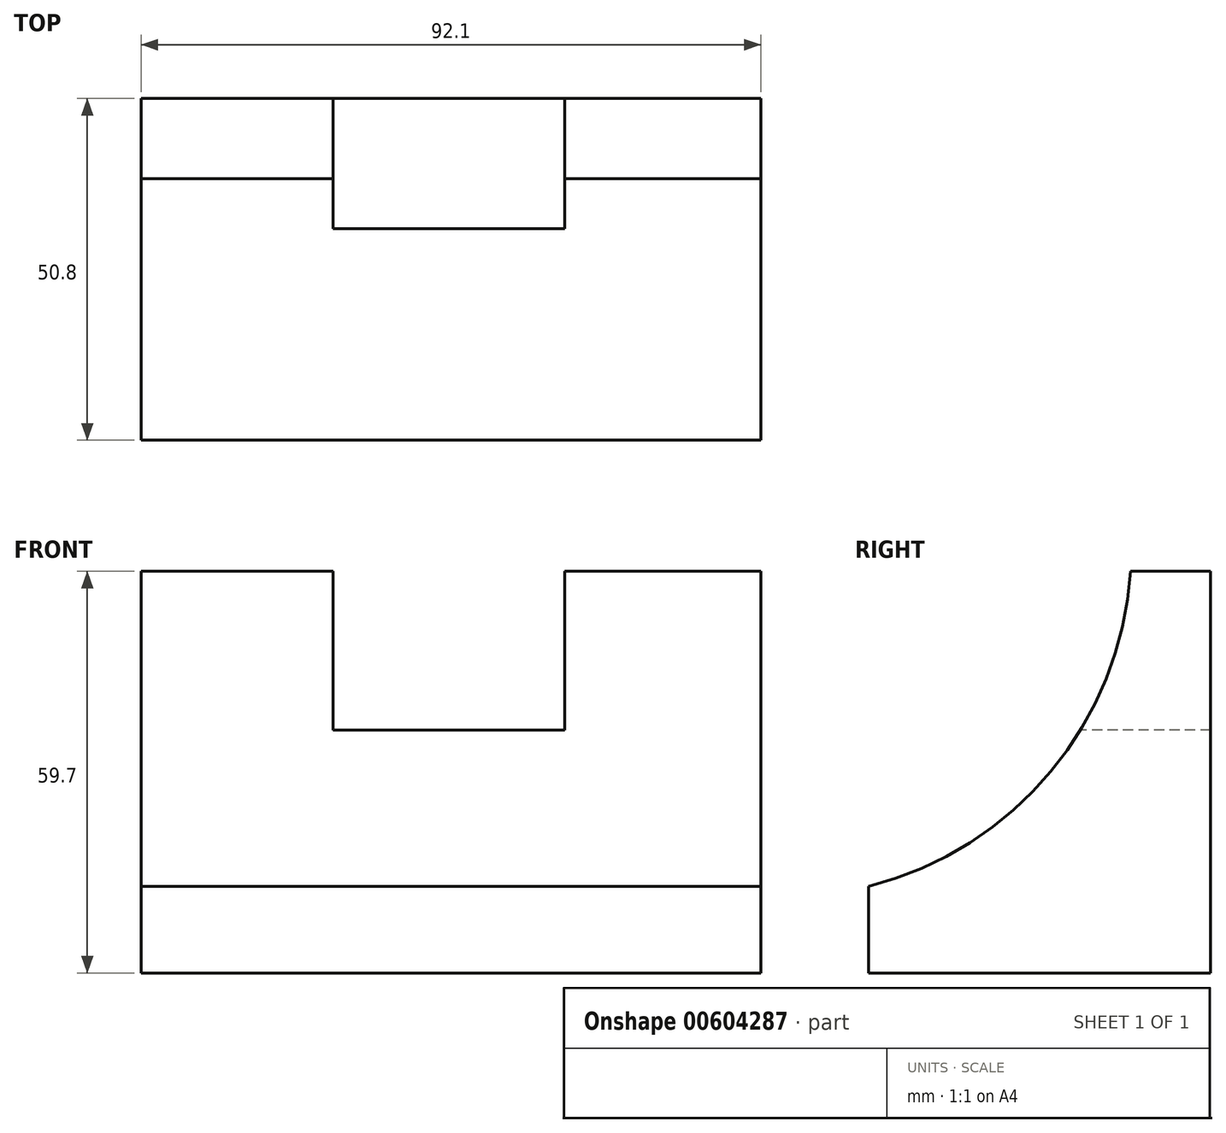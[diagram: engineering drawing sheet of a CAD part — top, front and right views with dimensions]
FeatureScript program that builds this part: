
annotation { "Feature Type Name" : "Feature", "Feature Type Description" : "" }
export const myFeature = defineFeature(function(context is Context, id is Id, definition is map)
    precondition{}
    {
        {
            var Q0;
            Q0=qCreatedBy(makeId("Front.planeOp"),FACE);
            var sketch = newSketch(context, id + "F0", { "sketchPlane" : qUnion([Q0])});
            skLineSegment(sketch, "E0.bottom", {"start": v(-72.72, 0) * mm, "end": v(19.38, 0) * mm});
            skLineSegment(sketch, "E0.top", {"start": v(-72.72, 59.7) * mm, "end": v(19.38, 59.7) * mm});
            skLineSegment(sketch, "E0.left", {"start": v(-72.72, 0) * mm, "end": v(-72.72, 59.7) * mm});
            skLineSegment(sketch, "E0.right", {"start": v(19.38, 0) * mm, "end": v(19.38, 59.7) * mm});
            skSolve(sketch);
        }
        {
            var Q0;
            Q0=makeQuery(id+"F0.imprint","IMPRINT",FACE,{"disambiguationData":[TD([[makeQuery(id+"F0.imprint","IMPRINT",EDGE,{"derivedFrom":sQuery(id+"F0.wireOp",EDGE,"E0.bottom")}),1.0]])]});
            extrude(context, id + "F1", {"entities" : qUnion([Q0]), "depth" : 25.4 * mm, "offsetDistance" : 25.4 * mm});
        }
        {
            var Q0;
            Q0=makeQuery(id+"F1.opExtrude","CAP_FACE",FACE,{"disambiguationData":[OSD([sQuery(id+"F0.wireOp",EDGE,"E0.bottom"),sQuery(id+"F0.wireOp",EDGE,"E0.top"),sQuery(id+"F0.wireOp",EDGE,"E0.left"),sQuery(id+"F0.wireOp",EDGE,"E0.right")])],"isStart":true});
            extrude(context, id + "F2", {"entities" : qUnion([Q0]), "operationType" : NewBodyOperationType.ADD, "depth" : 25.4 * mm, "offsetDistance" : 25.4 * mm});
        }
        {
            var Q0;
            {var subQ0=sQuery(id+"F0.wireOp",EDGE,"E0.right");Q0=makeQuery(id+"F2.boolean.opBoolean","MERGE",FACE,{"derivedFrom":[makeQuery(id+"F1.opExtrude","SWEPT_FACE",FACE,{"disambiguationData":[OSD([subQ0])]}),makeQuery(id+"F2.opExtrude","SWEPT_FACE",FACE,{"disambiguationData":[OSD([subQ0])]})]});}
            var sketch = newSketch(context, id + "F3", { "sketchPlane" : qUnion([Q0])});
            skArc(sketch, "E1", {"start": v(-25.4, 12.87) * mm, "mid": v(1.67, 29.95) * mm, "end": v(13.5, 59.7) * mm});
            skSolve(sketch);
        }
        {
            var Q0;
            Q0=makeQuery(id+"F1.opExtrude","CAP_FACE",FACE,{"disambiguationData":[OSD([sQuery(id+"F0.wireOp",EDGE,"E0.bottom"),sQuery(id+"F0.wireOp",EDGE,"E0.top"),sQuery(id+"F0.wireOp",EDGE,"E0.left"),sQuery(id+"F0.wireOp",EDGE,"E0.right")])],"isStart":false});
            var sketch = newSketch(context, id + "F4", { "sketchPlane" : qUnion([Q0])});
            skLineSegment(sketch, "E2", {"start": v(-44.2, 59.7) * mm, "end": v(-44.2, 36.13) * mm});
            skLineSegment(sketch, "E3", {"start": v(-44.2, 36.13) * mm, "end": v(-9.77, 36.13) * mm});
            skLineSegment(sketch, "E4", {"start": v(-9.77, 36.13) * mm, "end": v(-9.77, 59.7) * mm});
            skLineSegment(sketch, "E5", {"start": v(-9.77, 59.7) * mm, "end": v(-9.77, 36.13) * mm});
            skSolve(sketch);
        }
        {
            var Q0;
            {var subQ0=sQuery(id+"F4.wireOp",EDGE,"E2");Q0=makeQuery(id+"F4.imprint","IMPRINT",FACE,{"disambiguationData":[TD([[makeQuery(id+"F4.imprint","IMPRINT",EDGE,{"derivedFrom":subQ0}),1.0]])]});}
            extrude(context, id + "F5", {"entities" : qUnion([Q0]), "operationType" : NewBodyOperationType.REMOVE, "oppositeDirection" : true, "depth" : 70.61 * mm, "offsetDistance" : 25.4 * mm});
        }
        {
            var Q0;
            {var subQ0=sQuery(id+"F3.wireOp",EDGE,"E1");Q0=makeQuery(id+"F3.imprint","IMPRINT",FACE,{"disambiguationData":[TD([[makeQuery(id+"F3.imprint","IMPRINT",EDGE,{"derivedFrom":subQ0}),1.0]])]});}
            extrude(context, id + "F6", {"entities" : qUnion([Q0]), "operationType" : NewBodyOperationType.REMOVE, "oppositeDirection" : true, "depth" : 99.57 * mm, "offsetDistance" : 25.4 * mm});
        }
    });
